# Revit family: ГРЕЕРС ЗВ - 100 Е
name_source: partatom
category: Osprzęt elektryczny
revit_build: Autodesk Revit 2016 (Build: 20150220_1215(x64)
units: mm (PartAtom-declared; Revit-internal decimal feet)

## family parameters
Obiekt nadrzędny = Powierzchnia
Punkt obliczania pomieszczeń = Nie
Tnij formami wycięć po wczytaniu = Nie
Typ części = Normalny
Współdzielony = Nie
Wymiar okrągłego złącza = Użyj średnicy
Zachowaj orientację opisów = Nie

## types (6) — shared parameters
Domyślna rzędna = 2200 mm
IP = 21
Model = ГРЕЕРС ЗВ - 100 Е
Opis = Воздушная завеса
Producent = ГРЕЕРС
Автор = www.archispace.com
Вентилятор = Однофазный двигатель с поперечным ротором
Вес аппарата = 14.50 kg
Данные продукта = https://greers.ru
Длина = 1000 mm  [stored 3.28084 ft]
Классификация нагрузки = ДРУГОЕ
Коэффициент мощности = 1
Материал = ГРЕЕРС-сталь-белый
Материал 2 = ГРЕЕРС-сталь,перфорация-белый

## per-type parameters (varying)
| type | Количество фаз | Напряжение питания | Номинальный ток | Полная мощность | Тепловая мощность |
| ГРЕЕРС ЗВ - 100 Е, 1 скорость, 3x400B | 3 | 400 V | 9 A | 6072 VA | 6.1 kW |
| ГРЕЕРС ЗВ - 100 Е, 2 скорость, 3x400B | 3 | 400 V | 9 A | 6279 VA | 6.4 kW |
| ГРЕЕРС ЗВ - 100 Е, 3 скорость, 3x400B | 3 | 400 V | 9 A | 6486 VA | 6.5 kW |
| ГРЕЕРС ЗВ - 100 Е, 1 скорость, 1x230B | 1 | 230 V | 26 A | 6072 VA | 6.1 kW |
| ГРЕЕРС ЗВ - 100 Е, 2 скорость, 1x230B | 1 | 230 V | 27 A | 6279 VA | 6.4 kW |
| ГРЕЕРС ЗВ - 100 Е, 3 скорость, 1x230B | 1 | 230 V | 28 A | 6486 VA | 6.5 kW |

note: [stored X ft] marks values corroborated as IEEE doubles in the binary element streams (Revit-internal decimal feet)
